# Revit family: BuroSeating_Konfurb_Pala Barstool
name_source: partatom
category: Furniture
units: mm (PartAtom-declared; Revit-internal decimal feet)

## family parameters
Always vertical = Yes
Cut with Voids When Loaded = No
OmniClass Number = 23.40.70.14.64.11
OmniClass Title = Office Furniture
Room Calculation Point = No
Shared = No
Work Plane-Based = No

## types (7) — shared parameters
Assembly Code = E2020
BaseFrameMaterial = BuroSeating_Wood_Yellow Pine
BaseOffset = 6 mm  [stored 0.019685 ft]
FeetMaterial = BuroSeating_Plastic_Black
FootRestMaterial = BuroSeating_Aluminium_Black
Manufacturer = Buro Seating
NominalDepth = 510 mm  [stored 1.67323 ft]
NominalHeight = 820 mm  [stored 2.69029 ft]
NominalWidth = 440 mm  [stored 1.44357 ft]
ProductGroup = Konfurb Pala
ProductPageURL AU = https://buroseating.com
ProductPageURL NZ = https://buroseating.co.nz
ProductRange = Konfurb
SeatDepth = 350 mm  [stored 1.14829 ft]
SeatHeight = 730 mm  [stored 2.39501 ft]
SeatWidth = 350 mm  [stored 1.14829 ft]
URL = https://buroseating.co.nz
URL AU = https://buroseating.com
WarrantyDescription = Full 5 year guarantee (excluding upholstery)
zero-valued in all types: Default Elevation

## per-type parameters (varying)
| type | Description | Model | SeatFabric | SeatMaterial | SeatShell | SeatShellMaterial |
| Polypropylene Shell - Red | Konfurb Pala Barstool Polypropylene Shell - Grey | KON143-2 | No | <By Category> | Yes | BuroSeating_Polypropylene_Grey |
| Fabric Seat - Culp Dorset Grey | Konfurb Pala Barstool Polypropylene Shell - Custom | KON143-00 | Yes | BuroSeating_Fabric_Culp Dorset | No | BuroSeating_Polypropylene_Red |
| Polypropylene Shell - Black | Konfurb Pala Barstool Polypropylene Shell - Black | KON143-3 | No | BuroSeating_Fabric_Culp Dorset | Yes | BuroSeating_Polypropylene_Black |
| Polypropylene Shell - White | Konfurb Pala Barstool Polypropylene Shell - White | KON143-0 | No | BuroSeating_Fabric_Culp Dorset | Yes | BuroSeating_Polypropylene_White |
| Polypropylene Shell - Grey | Konfurb Pala Barstool Polypropylene Shell - Grey | KON143-2 | No | <By Category> | Yes | BuroSeating_Polypropylene_Grey |
| Fabric Seat - Custom | Konfurb Pala Barstool Polypropylene Shell - Culp Dorset Grey | KON143-82 | Yes | BuroSeating_Fabric_Culp Dorset | No | BuroSeating_Polypropylene_Red |
| Polypropylene Sell - Red | Konfurb Pala Barstool Polypropylene Shell (Red) | KON143-5 | No | BuroSeating_Polypropylene_Red | Yes | BuroSeating_Polypropylene_Red |

note: [stored X ft] marks values corroborated as IEEE doubles in the binary element streams (Revit-internal decimal feet)

## geometry (parser evidence)
native form markers: Sweep x11
no freeform markers — native parametric forms only
